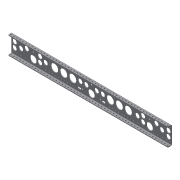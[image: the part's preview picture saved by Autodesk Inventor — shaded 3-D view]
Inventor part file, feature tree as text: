
AUTODESK INVENTOR PART (.ipt)
format: ipt  version: 2013 (Build 170138000, 138)  size: 327,168 bytes
history: native  units: in
note: dims shown in document units (in); Inventor stores cm internally (conversion verified against a paired STEP export)
features: chamfer x1, other x1, imported_body x1
ambient origin geometry x8: Origin, YZ Plane, XZ Plane, XY Plane, X Axis, Y Axis, Z Axis, Center Point
feature tree (3):
  chamfer  "Chamfer1"  [1 undecoded]
  other  "217-3648-001 Rev11"
  imported_body  "Base1"
note: 1 required parameter value undecoded (feature->parameter linkage not recoverable at this tier; creation-order binding heuristic only, values carry confidence <= 0.55)
